# Revit family: HL_Трап для внутренних помещений__HL310NPrR
name_source: partatom
category: Plumbing Fixtures
revit_build: Autodesk Revit Architecture 2016 (Build: 20150220_1215(x64)
units: mm (PartAtom-declared; Revit-internal decimal feet)

## family parameters
Always vertical = Yes
Cut with Voids When Loaded = No
OmniClass Number = 23.70.50.21.24.14
OmniClass Title = Deck Waste Water Drains
Part Type = Normal
Room Calculation Point = Yes
Round Connector Dimension = Use Diameter
Shared = Yes
Work Plane-Based = No

## types (1)
- HL310NPrR
    CW Connection = No
    Description = Трапы для внутренних помещений
    EAN = 9003076006052
    HW Connection = No
    Keynote = HL310NPrR
    Manufacturer = HL Hutterer & Lechner GmbH
    Model = HL310NPrR
    Type Comments = HL310NPrR Трап для внутренних помещений DN50/75/110 вертикальный с запахозапирающим устройством Primus, круглая насадка d 133мм/d 112мм
    URL = http://www.hutterer-lechner.com
    Vent Connection = No
    Waste Connection = Yes
    ВЕС = 0,65 [kg]
    ВЫСОТА МОНТАЖА = 164 mm
    МАКСИМАЛЬНАЯ НАГРУЗКА КЛАССА = K3 - 300 kg
    МАТЕРИАЛ = PE
    НАСАДКА = 20-75 mm / d 133 mm / PP-V2A
    ПРОИЗВОДИТЕЛЬНОСТЬ = 0,5 l/s
    ПРОПУСКНАЯ СПОСОБНОСТЬ = 0.5 L/s
    РАЗМЕР = DN50/75/110
    РЕШЁТКА = d 112 mm / V2A

## geometry (parser evidence)
native form markers: Sweep x30
no freeform markers — native parametric forms only
